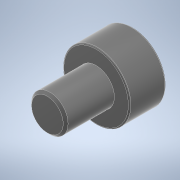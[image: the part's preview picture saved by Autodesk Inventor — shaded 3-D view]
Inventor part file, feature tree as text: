
AUTODESK INVENTOR PART (.ipt)
format: ipt  version: 2022 (Build 260153000, 153)  size: 143,872 bytes
history: native  units: in
note: dims shown in document units (in); Inventor stores cm internally (conversion verified against a paired STEP export)
features: sketch x3, extrude x2, plane x1, fillet x1, chamfer x1
ambient origin geometry x8: Origin, YZ Plane, XZ Plane, XY Plane, X Axis, Y Axis, Z Axis, Center Point
bodies: Body1 (feature_tree)
feature tree (8):
  plane  "Work Plane1"
  fillet  "Fillet1"  [1 undecoded]
  extrude  "Extrusion2"  Depth=0.0039in
  extrude  "Extrusion1"  Depth=0.1575in TaperAngle=0.0deg
  chamfer  "Chamfer1"  Distance=0.0079in
  sketch  "Sketch1"  dims[d1=0.1181in d2=0.0in d3=0.0039in]
  sketch  "Sketch2"  dims[d4=0.1181in d5=0.0in d6=0.1575in d7=0.0in d8=0.0079in d9=0.0079in d10=17.7165in]
  sketch  "Sketch3"
note: 1 required parameter value undecoded (feature->parameter linkage not recoverable at this tier; creation-order binding heuristic only, values carry confidence <= 0.55)
